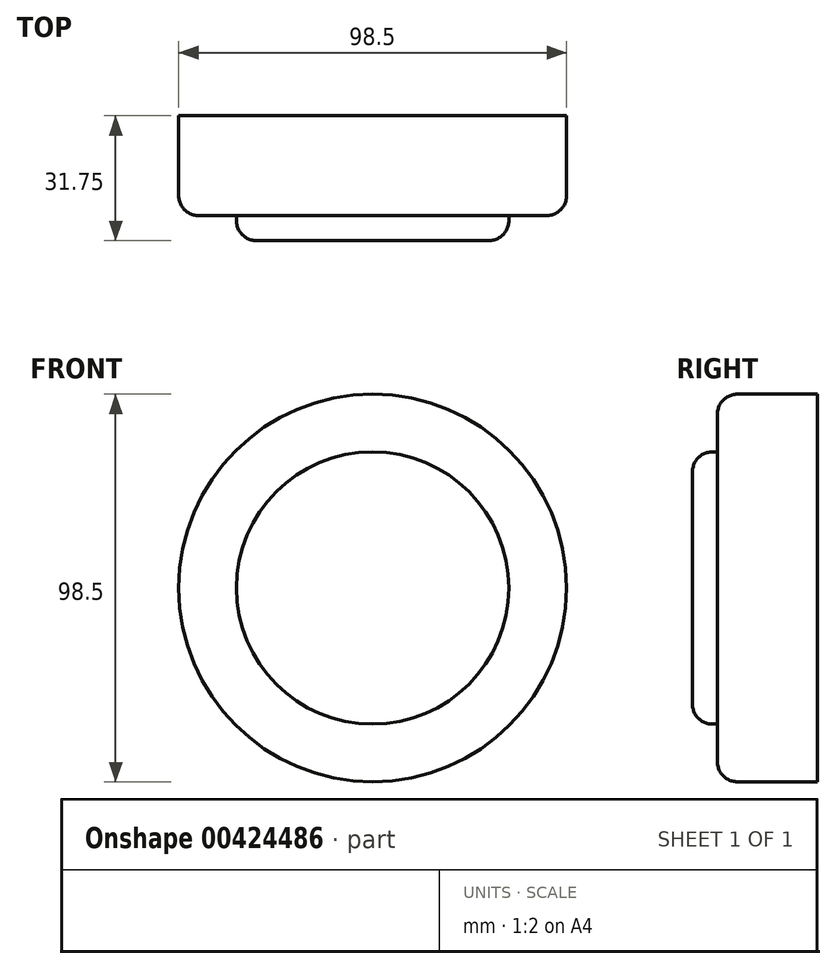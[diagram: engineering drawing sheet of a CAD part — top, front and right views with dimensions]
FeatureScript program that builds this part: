
annotation { "Feature Type Name" : "Feature", "Feature Type Description" : "" }
export const myFeature = defineFeature(function(context is Context, id is Id, definition is map)
    precondition{}
    {
        {
            var Q0;
            Q0=qCreatedBy(makeId("Front.planeOp"),FACE);
            var sketch = newSketch(context, id + "F0", { "sketchPlane" : qUnion([Q0])});
            skCircle(sketch, "E0", {"center": v(-40.6, 28.18) * mm, "radius": 34.6 * mm});
            skCircle(sketch, "E1", {"center": v(-40.6, 28.18) * mm, "radius": 49.25 * mm});
            skLineSegment(sketch, "E2", {"start": v(-75.2, 27.9) * mm, "end": v(-6, 27.9) * mm});
            skLineSegment(sketch, "E3", {"start": v(-40.6, 62.78) * mm, "end": v(-40.6, 28.18) * mm});
            skLineSegment(sketch, "E4", {"start": v(-40.6, -6.41) * mm, "end": v(-40.6, 28.18) * mm});
            skSolve(sketch);
        }
        {
            var Q0;
            {var subQ0=sQuery(id+"F0.wireOp",EDGE,"E2");var subQ1=sQuery(id+"F0.wireOp",EDGE,"E0");var subQ2=makeQuery(id+"F0.imprint","INTERSECT",VERTEX,{"disambiguationData":[OD(0.0)],"derivedFrom":[subQ1,subQ0]});Q0=makeQuery(id+"F0.imprint","IMPRINT",FACE,{"disambiguationData":[TD([[makeQuery(id+"F0.imprint","IMPRINT",EDGE,{"disambiguationData":[TD([[subQ2,-1.0]])],"derivedFrom":subQ1}),1.0]])]});}
            var Q1;
            {var subQ3=sQuery(id+"F0.wireOp",EDGE,"E3");Q1=makeQuery(id+"F0.imprint","IMPRINT",FACE,{"disambiguationData":[TD([[makeQuery(id+"F0.imprint","IMPRINT",EDGE,{"derivedFrom":subQ3}),-1.0]])]});}
            var Q2;
            {var subQ3=sQuery(id+"F0.wireOp",EDGE,"E3");Q2=makeQuery(id+"F0.imprint","IMPRINT",FACE,{"disambiguationData":[TD([[makeQuery(id+"F0.imprint","IMPRINT",EDGE,{"derivedFrom":subQ3}),1.0]])]});}
            var Q3;
            {var subQ0=sQuery(id+"F0.wireOp",EDGE,"E2");var subQ1=sQuery(id+"F0.wireOp",EDGE,"E0");var subQ2=makeQuery(id+"F0.imprint","INTERSECT",VERTEX,{"disambiguationData":[OD(1.0)],"derivedFrom":[subQ1,subQ0]});Q3=makeQuery(id+"F0.imprint","IMPRINT",FACE,{"disambiguationData":[TD([[makeQuery(id+"F0.imprint","IMPRINT",EDGE,{"disambiguationData":[TD([[subQ2,1.0]])],"derivedFrom":subQ1}),1.0]])]});}
            extrude(context, id + "F1", {"entities" : qUnion([Q0, Q1, Q2, Q3]), "depth" : 31.75 * mm});
        }
        {
            var Q0;
            Q0=makeQuery(id+"F0.imprint","IMPRINT",FACE,{"disambiguationData":[TD([[makeQuery(id+"F0.imprint","IMPRINT",EDGE,{"derivedFrom":sQuery(id+"F0.wireOp",EDGE,"E1")}),1.0]])]});
            extrude(context, id + "F2", {"entities" : qUnion([Q0]), "operationType" : NewBodyOperationType.ADD, "depth" : 25.4 * mm});
        }
        {
            var Q0;
            Q0=makeQuery(id+"F1.opExtrude","CAP_EDGE",EDGE,{"disambiguationData":[OSD([sQuery(id+"F0.wireOp",EDGE,"E0")])],"isStart":false});
            var Q1;
            Q1=makeQuery(id+"F2.opExtrude","CAP_EDGE",EDGE,{"disambiguationData":[OSD([sQuery(id+"F0.wireOp",EDGE,"E1")])],"isStart":false});
            fillet(context, id + "F3", {"entities" : qUnion([Q0, Q1]), "radius" : 5.08 * mm, "tangentPropagation" : true, "allowEdgeOverflow" : false});
        }
    });
